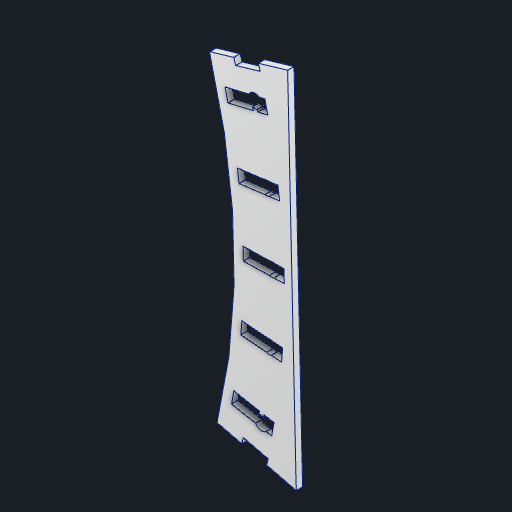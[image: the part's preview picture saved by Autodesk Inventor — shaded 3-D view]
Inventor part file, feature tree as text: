
AUTODESK INVENTOR PART (.ipt)
format: ipt  version: 2023 (Build 270158000, 158)  size: 325,120 bytes
history: native  units: in
note: dims shown in document units (in); Inventor stores cm internally (conversion verified against a paired STEP export)
features: reference x29, other x10, sketch x5, extrude x3, hole x2, plane x1
ambient origin geometry x8: Origin, YZ Plane, XZ Plane, XY Plane, X Axis, Y Axis, Z Axis, Center Point
bodies: Body1 (feature_tree)
feature tree (50):
  plane  "Work Plane2"
  extrude  "Extrusion3"  Depth=0.125in TaperAngle=0.0deg
  extrude  "Extrusion4"  Depth=0.5in
  hole  "Hole2"  [1 undecoded]
  extrude  "Extrusion5"  Depth=0.0656in
  hole  "Hole3"  [1 undecoded]
  sketch  "Sketch3"  dims[d7=0.125in d8=0.0in d21=0.125in d22=0.0in]
  reference  "Reference86"
  reference  "Reference87"
  reference  "Reference88"
  reference  "Reference89"
  reference  "Reference90"
  reference  "Reference91"
  reference  "Reference92"
  reference  "Reference93"
  reference  "Reference94"
  reference  "Reference95"
  reference  "Reference96"
  reference  "Reference97"
  reference  "Reference98"
  reference  "Reference99"
  reference  "Reference100"
  reference  "Reference101"
  reference  "Reference102"
  reference  "Reference103"
  reference  "Reference104"
  reference  "Reference105"
  reference  "Reference106"
  sketch  "Sketch5"  dims[d23=0.5in d24=0.5in]
  reference  "Reference111"
  reference  "Reference113"
  sketch  "Sketch6"  dims[d25=0.266in d26=0.75in d27=0.507in d28=0.25in d29=0.5635in d30=0.536in d31=0.0in d32=0.0656in]
  reference  "Reference115"
  reference  "Reference117"
  sketch  "Sketch7"  dims[d33=0.0656in d34=0.0656in]
  sketch  "Sketch8"  dims[d35=0.0656in d36=0.0656in d37=1.15in d38=0.45in d39=0.25in d40=0.5091in d41=0.45in d42=0.45in d43=0.45in d44=0.45in d45=0.25in d46=0.25in d47=0.25in d48=0.25in d49=0.5091in d50=0.5091in d51=0.5091in d52=0.5091in d53=0.125in d54=0.0in d55=0.4in d56=0.75in d57=0.75in d58=0.75in d59=0.266in d60=0.75in d61=0.507in d62=0.25in d63=0.5635in d64=0.536in d65=0.0in d66=0.25in d67=0.2in d68=0.0909in d69=0.25in d70=0.2in d71=0.25in d72=0.2in d73=0.25in d74=0.2in d75=0.25in d76=0.2in d77=0.0909in d78=0.0909in d79=0.0909in d80=0.0909in]
  reference  "Reference124"
  reference  "Reference125"
  reference  "Reference126"
  reference  "Reference127"
  other  "<userpath>\Desktop\WaccaController\Wacca Controller\Touch Segment\Touch Segment.iam"
  other  "Touch Segment.iam"
  other  "Touch Fifth:4"
  other  "Touch Fifth:3"
  other  "Touch Fifth:2"
  other  "Touch Fifth:1"
  other  "Touch Fifth:5"
  other  "SidePlate:2"
  other  "SidePlate:1"
  other  "<userpath>\Desktop\Wacca Controller V2\Touch Segment\Touch Segment.iam"
note: 2 required parameter values undecoded (feature->parameter linkage not recoverable at this tier; creation-order binding heuristic only, values carry confidence <= 0.55)
